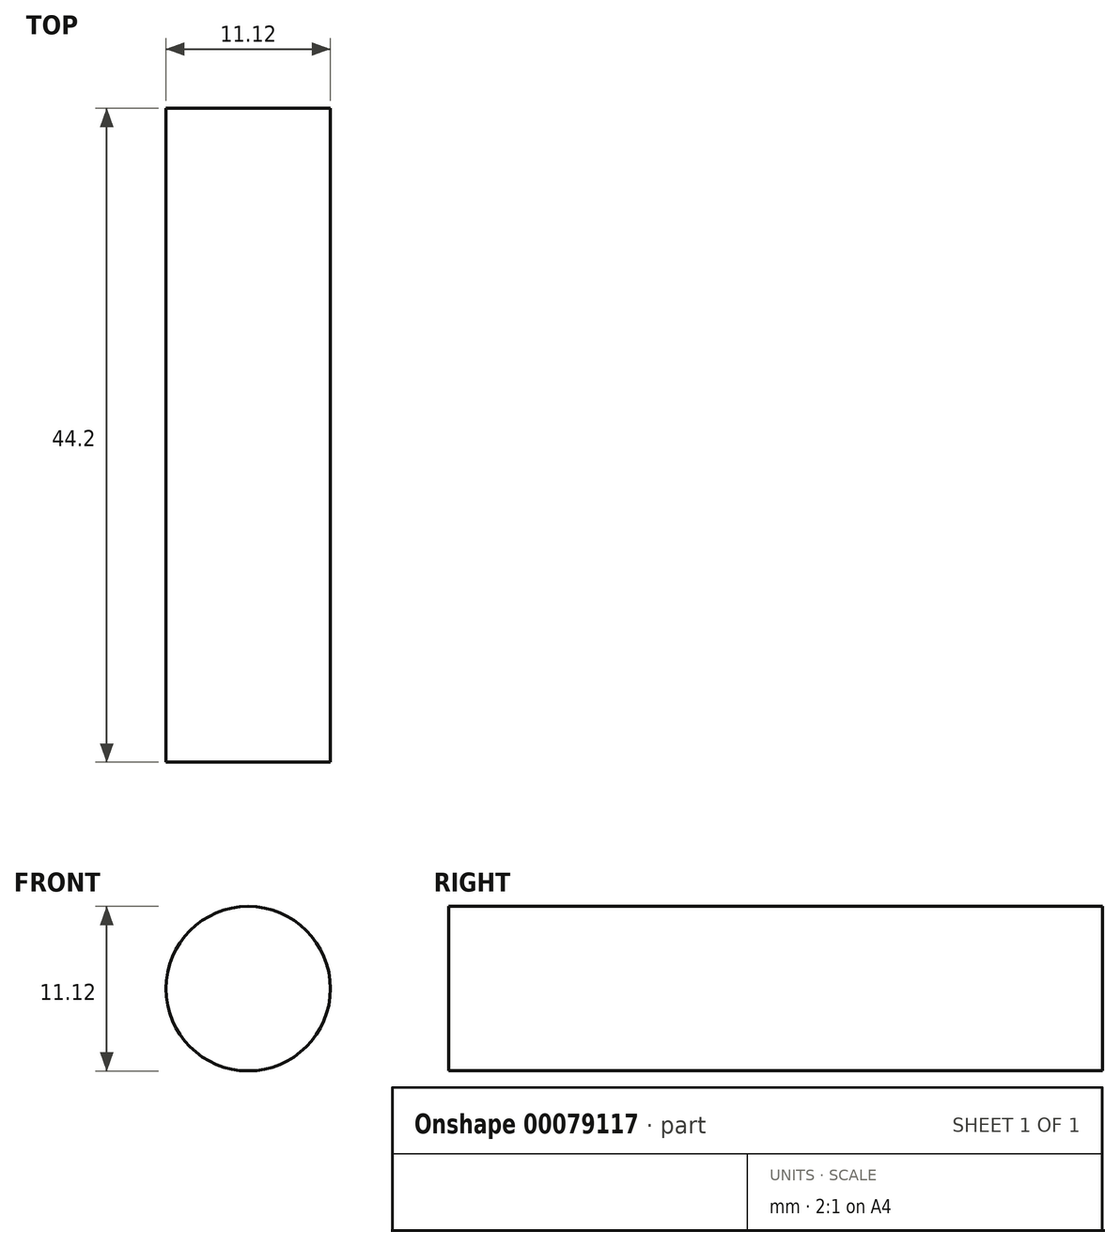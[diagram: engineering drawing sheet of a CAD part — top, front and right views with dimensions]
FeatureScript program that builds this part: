
annotation { "Feature Type Name" : "Feature", "Feature Type Description" : "" }
export const myFeature = defineFeature(function(context is Context, id is Id, definition is map)
    precondition{}
    {
        {
            var Q0;
            Q0=qCreatedBy(makeId("Front.planeOp"),FACE);
            var sketch = newSketch(context, id + "F0", { "sketchPlane" : qUnion([Q0])});
            skCircle(sketch, "E0", {"center": v(0, 0) * mm, "radius": 5.56 * mm});
            skSolve(sketch);
        }
        {
            var Q0;
            Q0 = qSketchRegion(id + "F0", true);
            extrude(context, id + "F1", {"entities" : qUnion([Q0]), "depth" : 44.2 * mm});
        }
    });
